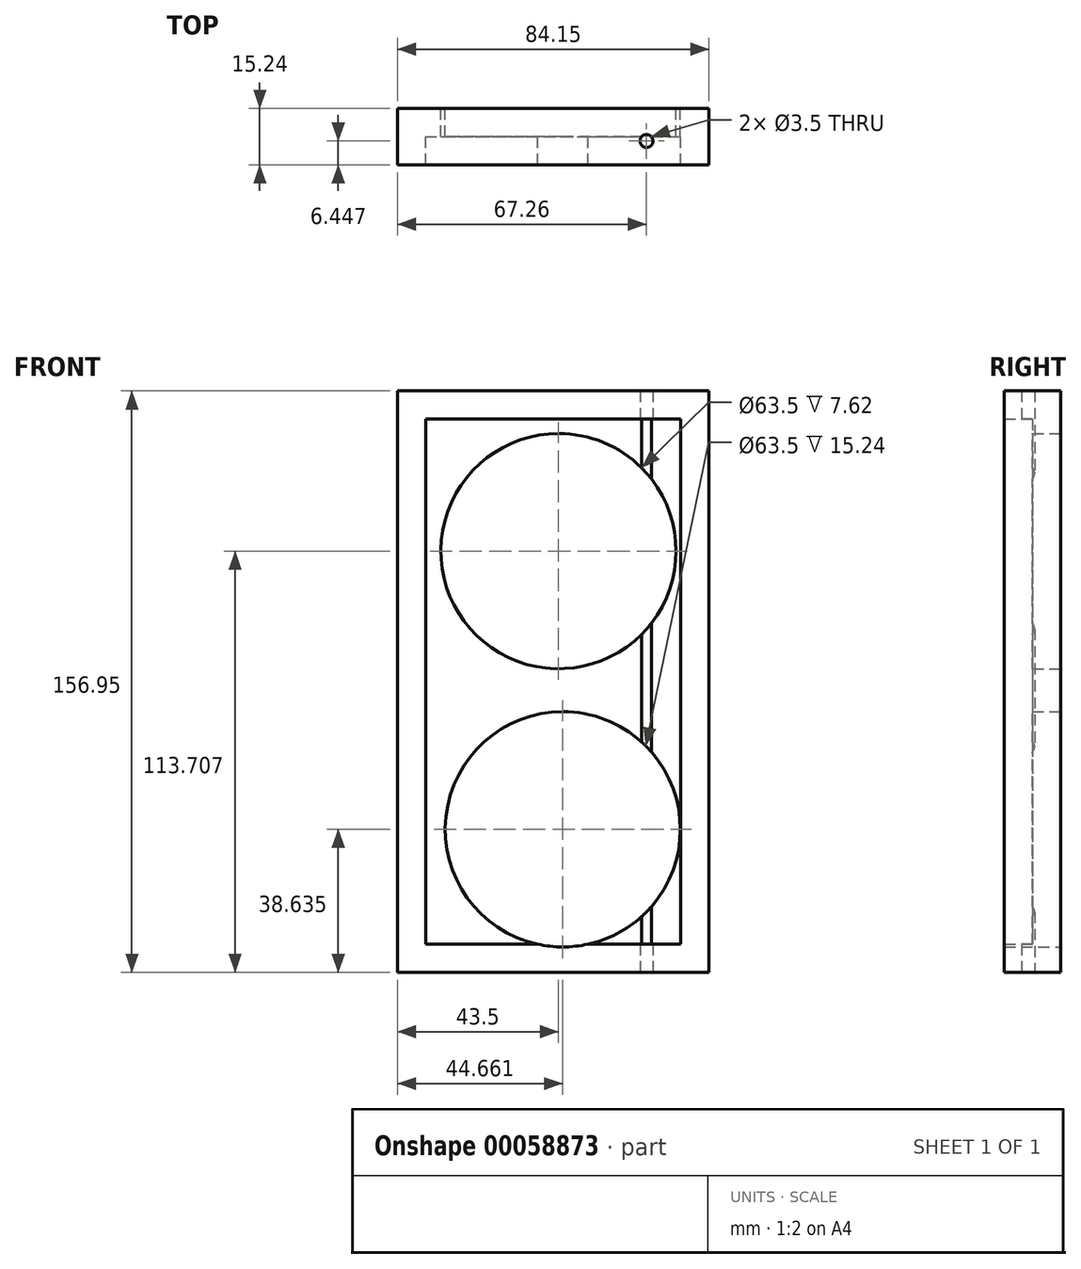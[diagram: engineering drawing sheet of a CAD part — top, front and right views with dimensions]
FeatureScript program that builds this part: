
annotation { "Feature Type Name" : "Feature", "Feature Type Description" : "" }
export const myFeature = defineFeature(function(context is Context, id is Id, definition is map)
    precondition{}
    {
        {
            var Q0;
            Q0=qCreatedBy(makeId("Front.planeOp"),FACE);
            var sketch = newSketch(context, id + "F0", { "sketchPlane" : qUnion([Q0])});
            skLineSegment(sketch, "E0.bottom", {"start": v(-67.26, 80.93) * mm, "end": v(16.9, 80.93) * mm});
            skLineSegment(sketch, "E0.top", {"start": v(-67.26, -76.02) * mm, "end": v(16.9, -76.02) * mm});
            skLineSegment(sketch, "E0.left", {"start": v(-67.26, 80.93) * mm, "end": v(-67.26, -76.02) * mm});
            skLineSegment(sketch, "E0.right", {"start": v(16.9, 80.93) * mm, "end": v(16.9, -76.02) * mm});
            skSolve(sketch);
        }
        {
            var Q0;
            Q0=makeQuery(id+"F0.imprint","IMPRINT",FACE,{"disambiguationData":[TD([[makeQuery(id+"F0.imprint","IMPRINT",EDGE,{"derivedFrom":sQuery(id+"F0.wireOp",EDGE,"E0.bottom")}),-1.0]])]});
            extrude(context, id + "F1", {"entities" : qUnion([Q0]), "depth" : 15.24 * mm});
        }
        {
            var Q0;
            Q0=makeQuery(id+"F1.opExtrude","CAP_FACE",FACE,{"disambiguationData":[OSD([sQuery(id+"F0.wireOp",EDGE,"E0.bottom"),sQuery(id+"F0.wireOp",EDGE,"E0.top"),sQuery(id+"F0.wireOp",EDGE,"E0.left"),sQuery(id+"F0.wireOp",EDGE,"E0.right")])],"isStart":false});
            shell(context, id + "F2", {"entities" : qUnion([Q0]), "thickness" : 7.62 * mm});
        }
        {
            var Q0;
            Q0=makeQuery(id+"F1.opExtrude","CAP_FACE",FACE,{"disambiguationData":[OSD([sQuery(id+"F0.wireOp",EDGE,"E0.bottom"),sQuery(id+"F0.wireOp",EDGE,"E0.top"),sQuery(id+"F0.wireOp",EDGE,"E0.left"),sQuery(id+"F0.wireOp",EDGE,"E0.right")])],"isStart":true});
            var sketch = newSketch(context, id + "F3", { "sketchPlane" : qUnion([Q0])});
            skPoint(sketch, "E1", {"position": v(23.76, 37.69) * mm});
            skPoint(sketch, "E2", {"position": v(23.76, -31.58) * mm});
            skSolve(sketch);
        }
        {
            var Q0;
            Q0=sQuery(id+"F3.wireOp",VERTEX,"E1");
            var Q1;
            Q1=makeQuery(id+"F1.opExtrude","SWEPT_BODY",BODY,{"disambiguationData":[OSD([sQuery(id+"F0.wireOp",EDGE,"E0.bottom"),sQuery(id+"F0.wireOp",EDGE,"E0.top"),sQuery(id+"F0.wireOp",EDGE,"E0.left"),sQuery(id+"F0.wireOp",EDGE,"E0.right")])]});
            hole(context, id + "F4", {"style" : HoleStyle.SIMPLE, "holeDiameter" : 63.5 * mm, "endStyle" : HoleEndStyle.THROUGH, "locations" : qUnion([Q0]), "scope" : qUnion([Q1])});
        }
        {
            var Q0;
            Q0=makeQuery(id+"F1.opExtrude","CAP_FACE",FACE,{"disambiguationData":[OSD([sQuery(id+"F0.wireOp",EDGE,"E0.bottom"),sQuery(id+"F0.wireOp",EDGE,"E0.top"),sQuery(id+"F0.wireOp",EDGE,"E0.left"),sQuery(id+"F0.wireOp",EDGE,"E0.right")])],"isStart":true});
            var sketch = newSketch(context, id + "F5", { "sketchPlane" : qUnion([Q0])});
            skPoint(sketch, "E3", {"position": v(22.6, -37.39) * mm});
            skSolve(sketch);
        }
        {
            var Q0;
            Q0=sQuery(id+"F5.wireOp",VERTEX,"E3");
            var Q1;
            Q1=makeQuery(id+"F1.opExtrude","SWEPT_BODY",BODY,{"disambiguationData":[OSD([sQuery(id+"F0.wireOp",EDGE,"E0.bottom"),sQuery(id+"F0.wireOp",EDGE,"E0.top"),sQuery(id+"F0.wireOp",EDGE,"E0.left"),sQuery(id+"F0.wireOp",EDGE,"E0.right")])]});
            hole(context, id + "F6", {"style" : HoleStyle.SIMPLE, "holeDiameter" : 63.5 * mm, "endStyle" : HoleEndStyle.THROUGH, "locations" : qUnion([Q0]), "scope" : qUnion([Q1])});
        }
        {
            var Q0;
            Q0=makeQuery(id+"F1.opExtrude","SWEPT_FACE",FACE,{"disambiguationData":[OSD([sQuery(id+"F0.wireOp",EDGE,"E0.top")])]});
            var sketch = newSketch(context, id + "F7", { "sketchPlane" : qUnion([Q0])});
            skPoint(sketch, "E4", {"position": v(0, 8.8) * mm});
            skSolve(sketch);
        }
        {
            var Q0;
            Q0=sQuery(id+"F7.wireOp",VERTEX,"E4");
            var Q1;
            Q1=makeQuery(id+"F1.opExtrude","SWEPT_BODY",BODY,{"disambiguationData":[OSD([sQuery(id+"F0.wireOp",EDGE,"E0.bottom"),sQuery(id+"F0.wireOp",EDGE,"E0.top"),sQuery(id+"F0.wireOp",EDGE,"E0.left"),sQuery(id+"F0.wireOp",EDGE,"E0.right")])]});
            hole(context, id + "F8", {"style" : HoleStyle.SIMPLE, "holeDiameter" : 3.5 * mm, "endStyle" : HoleEndStyle.THROUGH, "locations" : qUnion([Q0]), "scope" : qUnion([Q1])});
        }
    });
